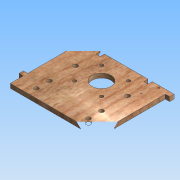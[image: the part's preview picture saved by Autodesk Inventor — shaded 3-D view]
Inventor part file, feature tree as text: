
AUTODESK INVENTOR PART (.ipt)
format: ipt  version: 2015 (Build 190159000, 159)  size: 299,520 bytes
history: native  units: mm
features: sketch x10, extrude x9, other x5, hole x3, projected_geometry x2, reference x2
ambient origin geometry x8: Origin, YZ Plane, XZ Plane, XY Plane, X Axis, Y Axis, Z Axis, Center Point
bodies: Body1 (feature_tree)
feature tree (31):
  other  "Blocks"
  extrude  "Extrusion2"  Depth=50.0mm
  hole  "Hole4"  [1 undecoded]
  hole  "Hole5"  [1 undecoded]
  hole  "Hole8"  [1 undecoded]
  extrude  "Extrusion11"  Depth=5.0mm
  extrude  "Extrusion12"  Depth=60.0mm
  extrude  "Extrusion13"  Depth=10.0mm
  sketch  "Sketch47"  dims[d78=22.0mm d79=6.0mm d80=4.0mm d81=2.0mm d82=90.0deg d83=2.0mm d84=0.0mm d176=30.0mm]
  extrude  "Extrusion14"  Depth=1.0mm
  extrude  "Extrusion15"  Depth=5.0mm
  extrude  "Extrusion16"  Depth=5.0mm TaperAngle=0.0deg
  extrude  "Extrusion17"  Depth=5.0mm TaperAngle=0.0deg
  extrude  "Extrusion18"  Depth=1.0mm
  sketch  "Sketch13"  dims[d21=100.0mm d22=50.0mm]
  sketch  "Sketch16"  dims[d23=5.0mm d24=0.0mm d43=31.0mm]
  sketch  "Sketch17"  dims[d44=31.0mm]
  other  "Block1"
  other  "Block2"
  other  "Block3"
  other  "Block4"
  projected_geometry  "Projected Loop3"
  sketch  "Sketch45"  dims[d45=4.0mm d46=6.0mm d47=4.0mm d48=2.0mm d49=90.0deg d50=4.0mm d51=0.0mm d52=60.0mm]
  projected_geometry  "Projected Loop4"
  reference  "Reference1"
  reference  "Reference2"
  sketch  "Sketch46"  dims[d53=5.2mm d54=6.0mm d55=4.0mm d56=2.0mm d57=90.0deg d58=4.0mm d59=0.0mm]
  sketch  "Sketch48"  dims[d179=5.0mm d184=5.0mm]
  sketch  "Sketch49"  dims[d185=10.0mm d189=60.0mm]
  sketch  "Sketch50"  dims[d190=30.0mm d191=10.0mm]
  sketch  "Sketch51"  dims[d192=5.0mm d193=15.0mm d196=5.0mm d197=5.0mm d198=0.0mm d200=5.0mm d201=0.0mm d202=47.0mm d203=5.0mm d204=5.0mm d205=20.0mm d206=5.0mm d207=5.0mm d208=20.0mm d209=10.0mm d210=0.0mm d211=2.0mm d212=2.5mm d213=10.0mm d214=2.0mm d215=10.0mm d216=2.5mm d217=10.0mm d218=0.0mm d219=10.0mm d220=0.0mm d221=5.0mm d222=5.0mm d223=5.0mm d224=5.0mm d225=5.0mm d226=0.0mm d227=5.0mm d228=5.0mm d230=5.0mm d231=0.0mm d232=5.0mm d233=5.0mm d235=5.0mm d236=0.0mm d239=60.0mm d240=60.0mm d29=1.0mm d30=1.0mm]
note: 3 required parameter values undecoded (feature->parameter linkage not recoverable at this tier; creation-order binding heuristic only, values carry confidence <= 0.55)
